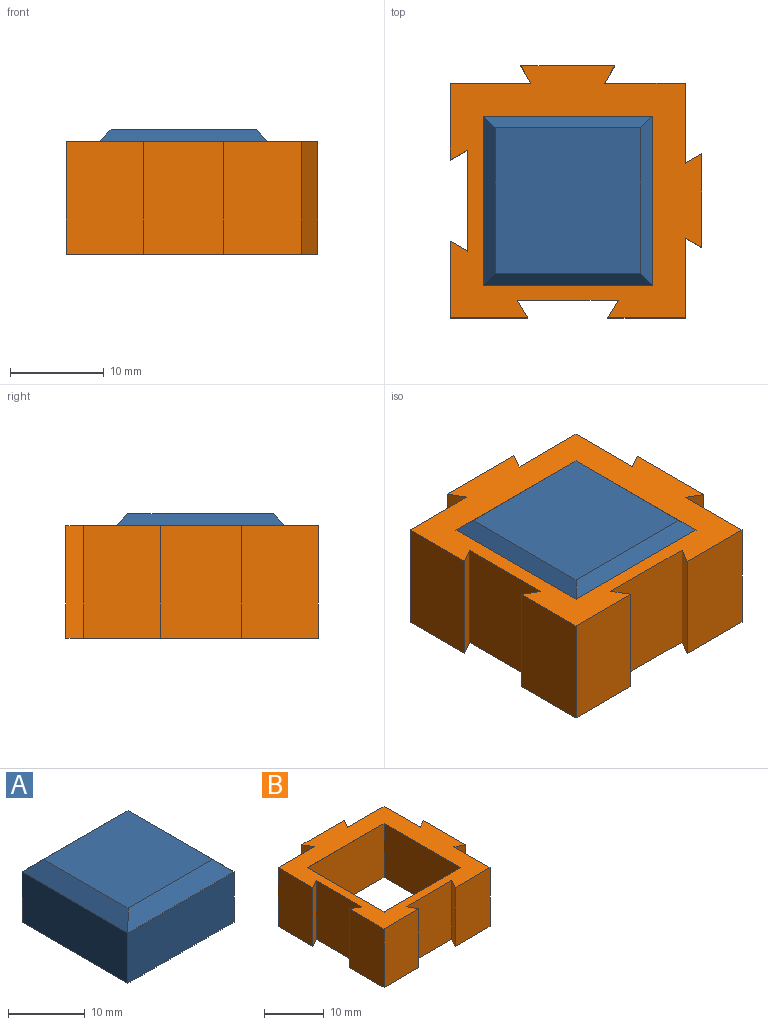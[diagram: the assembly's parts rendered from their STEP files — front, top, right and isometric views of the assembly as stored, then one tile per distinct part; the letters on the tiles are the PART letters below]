
ASSEMBLY  parts=2 mates=1
PART A: 23 faces, bbox 19.5x19.5x10 mm
  f0: plane 19.5x19.5mm, normal (0,0,-1), area 74mm2, adj f1,f2,f3,f4,f10,f11,f12,f13
  f1: plane 19.5x8mm, normal (0,-1,0), area 156mm2, adj f0,f2,f4,f7
  f2: plane 19.5x8mm, normal (1,0,0), area 156mm2, adj f0,f1,f3,f6
  f3: plane 19.5x8mm, normal (0,1,0), area 156mm2, adj f0,f2,f4,f8
  f4: plane 19.5x8mm, normal (-1,0,0), area 156mm2, adj f0,f1,f3,f9
  f5: plane 15.5x15.5mm, normal (0,0,1), area 240.3mm2, adj f6,f7,f8,f9
  f6: plane 19.5x2mm, normal (0.71,0,0.71), area 49.5mm2, adj f2,f5,f7,f8
  f7: plane 19.5x2mm, normal (0,-0.71,0.71), area 49.5mm2, adj f1,f5,f6,f9
  f8: plane 19.5x2mm, normal (0,0.71,0.71), area 49.5mm2, adj f3,f5,f6,f9
  f9: plane 19.5x2mm, normal (-0.71,0,0.71), area 49.5mm2, adj f4,f5,f7,f8
  f10: plane 17.5x7.59mm, normal (0,1,0), area 132.8mm2, adj f0,f11,f13,f16
  f11: plane 17.5x7.59mm, normal (-1,0,0), area 132.8mm2, adj f0,f10,f12,f15
  f12: plane 17.5x7.59mm, normal (0,-1,0), area 132.8mm2, adj f0,f11,f13,f17
  f13: plane 17.5x7.59mm, normal (1,0,0), area 132.8mm2, adj f0,f10,f12,f18
  f14: plane 14.67x14.67mm, normal (0,0,-1), area 174mm2, adj f15,f16,f17,f18,f20
  f15: plane 17.5x1.41mm, normal (-0.71,0,-0.71), area 32.2mm2, adj f11,f14,f16,f17
  f16: plane 17.5x1.41mm, normal (0,0.71,-0.71), area 32.2mm2, adj f10,f14,f15,f18
  f17: plane 17.5x1.41mm, normal (0,-0.71,-0.71), area 32.2mm2, adj f12,f14,f15,f18
  f18: plane 17.5x1.41mm, normal (0.71,0,-0.71), area 32.2mm2, adj f13,f14,f16,f17
  f19: cylinder r=3.12mm len=6.25mm, axis (0,0,1), area 49.1mm2, adj f21,f22
  f20: cylinder r=3.62mm len=7.25mm, axis (0,0,1), area 56.9mm2, adj f14,f21
  f21: plane 7.25x7.25mm, normal (0,0,-1), area 10.6mm2, adj f19,f20
  f22: plane 6.25x6.25mm, normal (0,0,-1), area 30.7mm2, adj f19
PART B: 30 faces, bbox 26.8x26.9x12 mm
  f0: plane 20x11mm, normal (0,1,0), area 220mm2, adj f4,f25,f27,f29
  f1: plane 20x11mm, normal (0,-1,0), area 220mm2, adj f4,f25,f27,f28
  f2: plane 20x1mm, normal (-0.71,0,-0.71), area 26.9mm2, adj f25,f26,f28,f29
  f3: plane 20x1mm, normal (0.71,0,-0.71), area 26.9mm2, adj f4,f26,f28,f29
  f4: plane 20x11mm, normal (1,0,0), area 220mm2, adj f0,f1,f3,f27
  f5: plane 12x1.75mm, normal (-0.5,0.87,0), area 24.2mm2, adj f6,f24,f26,f27
  f6: plane 12x8.51mm, normal (1,0,0), area 102.1mm2, adj f5,f7,f26,f27
  f7: plane 12x8.57mm, normal (0,1,0), area 102.8mm2, adj f6,f8,f26,f27
  f8: plane 12x1.85mm, normal (0.87,-0.5,0), area 25.6mm2, adj f7,f9,f26,f27
  f9: plane 12x10mm, normal (0,1,0), area 120mm2, adj f8,f10,f26,f27
  f10: plane 12x1.85mm, normal (-0.87,-0.5,0), area 25.6mm2, adj f9,f11,f26,f27
  f11: plane 12x8.57mm, normal (0,1,0), area 102.8mm2, adj f10,f12,f26,f27
  f12: plane 12x8.19mm, normal (-1,0,0), area 98.3mm2, adj f11,f13,f26,f27
  f13: plane 12x1.85mm, normal (0.5,-0.87,0), area 25.6mm2, adj f12,f14,f26,f27
  f14: plane 12x10.75mm, normal (-1,0,0), area 129mm2, adj f13,f15,f26,f27
  f15: plane 12x1.85mm, normal (0.5,0.87,0), area 25.6mm2, adj f14,f16,f26,f27
  f16: plane 12x8.19mm, normal (-1,0,0), area 98.3mm2, adj f15,f17,f26,f27
  f17: plane 12x8.22mm, normal (0,-1,0), area 98.7mm2, adj f16,f18,f26,f27
  f18: plane 12x1.9mm, normal (0.87,0.5,0), area 26.3mm2, adj f17,f19,f26,f27
  f19: plane 12x10.75mm, normal (0,-1,0), area 129mm2, adj f18,f20,f26,f27
  f20: plane 12x1.9mm, normal (-0.87,0.5,0), area 26.3mm2, adj f19,f21,f26,f27
  f21: plane 12x8.22mm, normal (0,-1,0), area 98.7mm2, adj f20,f22,f26,f27
  f22: plane 12x8.51mm, normal (1,0,0), area 102.1mm2, adj f21,f23,f26,f27
  f23: plane 12x1.75mm, normal (-0.5,-0.87,0), area 24.2mm2, adj f22,f24,f26,f27
  f24: plane 12x10mm, normal (1,0,0), area 120mm2, adj f5,f23,f26,f27
  f25: plane 20x11mm, normal (-1,0,0), area 220mm2, adj f0,f1,f2,f27
  f26: plane 26.85x26.75mm, normal (0,0,1), area 297mm2, adj f2,f3,f5,f6,f7,f8,f9,f10
  f27: plane 26.85x26.75mm, normal (0,0,-1), area 221mm2, adj f0,f1,f4,f5,f6,f7,f8,f9
  f28: plane 20x1mm, normal (0,-0.71,-0.71), area 26.9mm2, adj f1,f2,f3,f26
  f29: plane 20x1mm, normal (0,0.71,-0.71), area 26.9mm2, adj f0,f2,f3,f26
PLACE A rot(axis=(-0.14,0.81,-0.57),0deg) t=(-9.17,-2.87,0.89)mm
PLACE B t=(-9.17,-2.87,-2.36)mm fixed
MATE slider B.f27 <-> A.f0  axis (0,0,-1) through (-19.17,-12.87,-2.36)mm
